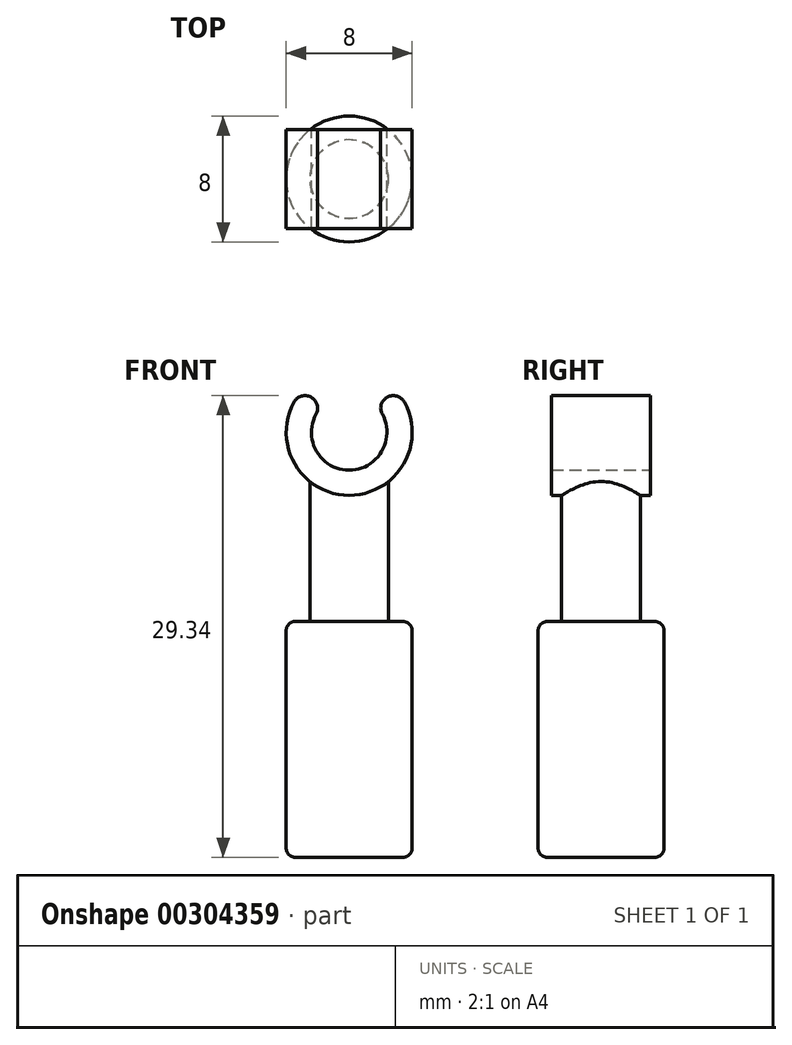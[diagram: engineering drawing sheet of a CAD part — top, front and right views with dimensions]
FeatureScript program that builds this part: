
annotation { "Feature Type Name" : "Feature", "Feature Type Description" : "" }
export const myFeature = defineFeature(function(context is Context, id is Id, definition is map)
    precondition{}
    {
        {
            var Q0;
            Q0=qCreatedBy(makeId("Front.planeOp"),FACE);
            var sketch = newSketch(context, id + "F0", { "sketchPlane" : qUnion([Q0])});
            skLineSegment(sketch, "E0", {"start": v(0, 25.03) * mm, "end": v(0, -25.74) * mm, "construction": true});
            skLineSegment(sketch, "E1", {"start": v(0, 0) * mm, "end": v(4, 0) * mm});
            skLineSegment(sketch, "E2", {"start": v(4, 0) * mm, "end": v(4, 15) * mm});
            skLineSegment(sketch, "E3", {"start": v(4, 15) * mm, "end": v(2.5, 15) * mm});
            skLineSegment(sketch, "E4", {"start": v(2.5, 15) * mm, "end": v(2.5, 24.5) * mm});
            skLineSegment(sketch, "E5", {"start": v(2.5, 24.5) * mm, "end": v(0, 24.5) * mm});
            skLineSegment(sketch, "E6", {"start": v(0, 24.5) * mm, "end": v(0, 0) * mm});
            skSolve(sketch);
        }
        {
            var Q0;
            Q0=makeQuery(id+"F0.imprint","IMPRINT",FACE,{"disambiguationData":[TD([[makeQuery(id+"F0.imprint","IMPRINT",EDGE,{"derivedFrom":sQuery(id+"F0.wireOp",EDGE,"E1")}),1.0]])]});
            var Q1;
            Q1=sQuery(id+"F0.wireOp",EDGE,"E0");
            revolve(context, id + "F1", {"entities" : qUnion([Q0]), "axis" : qUnion([Q1]), "revolveType" : RevolveType.FULL});
        }
        {
            var Q0;
            Q0=qCreatedBy(makeId("Front.planeOp"),FACE);
            var sketch = newSketch(context, id + "F2", { "sketchPlane" : qUnion([Q0])});
            skCircle(sketch, "E7", {"center": v(0, 27) * mm, "radius": 4 * mm});
            skCircle(sketch, "E8", {"center": v(0, 27) * mm, "radius": 2.4 * mm});
            skLineSegment(sketch, "E9", {"start": v(0, 34.38) * mm, "end": v(0, 20.92) * mm, "construction": true});
            skLineSegment(sketch, "E10", {"start": v(0, 27.65) * mm, "end": v(1.75, 28.64) * mm});
            skLineSegment(sketch, "E11", {"start": v(1.75, 28.64) * mm, "end": v(2.92, 29.74) * mm});
            skLineSegment(sketch, "E12", {"start": v(2.92, 29.74) * mm, "end": v(0, 32.85) * mm});
            skLineSegment(sketch, "E13", {"start": v(0, 32.85) * mm, "end": v(-2.92, 29.74) * mm});
            skLineSegment(sketch, "E14", {"start": v(-2.92, 29.74) * mm, "end": v(-1.75, 28.64) * mm});
            skLineSegment(sketch, "E15", {"start": v(-1.75, 28.64) * mm, "end": v(0, 27.65) * mm});
            skLineSegment(sketch, "E16", {"start": v(-1.75, 28.64) * mm, "end": v(0, 28.64) * mm, "construction": true});
            skLineSegment(sketch, "E17", {"start": v(1.75, 28.64) * mm, "end": v(0, 28.64) * mm, "construction": true});
            skLineSegment(sketch, "E18", {"start": v(-1.75, 28.64) * mm, "end": v(1.75, 28.64) * mm, "construction": true});
            skSolve(sketch);
        }
        {
            var Q0;
            {var subQ0=sQuery(id+"F2.wireOp",EDGE,"E11");Q0=makeQuery(id+"F2.imprint","IMPRINT",FACE,{"disambiguationData":[TD([[makeQuery(id+"F2.imprint","IMPRINT",EDGE,{"derivedFrom":subQ0}),-1.0]])]});}
            extrude(context, id + "F3", {"entities" : qUnion([Q0]), "operationType" : NewBodyOperationType.ADD, "endBound" : BoundingType.SYMMETRIC, "depth" : 6.3 * mm});
        }
        {
            var Q0;
            Q0=makeQuery(id+"F3.opExtrude","SWEPT_EDGE",EDGE,{"disambiguationData":[OSD([sQuery(id+"F2.wireOp",EDGE,"E7"),sQuery(id+"F2.wireOp",EDGE,"E11"),sQuery(id+"F2.wireOp",EDGE,"E12")])]});
            var Q1;
            Q1=makeQuery(id+"F3.opExtrude","SWEPT_EDGE",EDGE,{"disambiguationData":[OSD([sQuery(id+"F2.wireOp",EDGE,"E8"),sQuery(id+"F2.wireOp",EDGE,"E10"),sQuery(id+"F2.wireOp",EDGE,"E11")])]});
            var Q2;
            Q2=makeQuery(id+"F3.opExtrude","SWEPT_EDGE",EDGE,{"disambiguationData":[OSD([sQuery(id+"F2.wireOp",EDGE,"E8"),sQuery(id+"F2.wireOp",EDGE,"E14"),sQuery(id+"F2.wireOp",EDGE,"E15")])]});
            var Q3;
            Q3=makeQuery(id+"F3.opExtrude","SWEPT_EDGE",EDGE,{"disambiguationData":[OSD([sQuery(id+"F2.wireOp",EDGE,"E7"),sQuery(id+"F2.wireOp",EDGE,"E13"),sQuery(id+"F2.wireOp",EDGE,"E14")])]});
            fillet(context, id + "F4", {"entities" : qUnion([Q0, Q1, Q2, Q3]), "radius" : 0.8 * mm, "tangentPropagation" : true, "allowEdgeOverflow" : false});
        }
        {
            var Q0;
            Q0=makeQuery(id+"F1.opRevolve","SWEPT_EDGE",EDGE,{"disambiguationData":[OSD([sQuery(id+"F0.wireOp",EDGE,"E1"),sQuery(id+"F0.wireOp",EDGE,"E2")])]});
            var Q1;
            Q1=makeQuery(id+"F1.opRevolve","SWEPT_EDGE",EDGE,{"disambiguationData":[OSD([sQuery(id+"F0.wireOp",EDGE,"E2"),sQuery(id+"F0.wireOp",EDGE,"E3")])]});
            fillet(context, id + "F5", {"entities" : qUnion([Q0, Q1]), "radius" : 0.6 * mm, "tangentPropagation" : true, "allowEdgeOverflow" : false});
        }
    });
